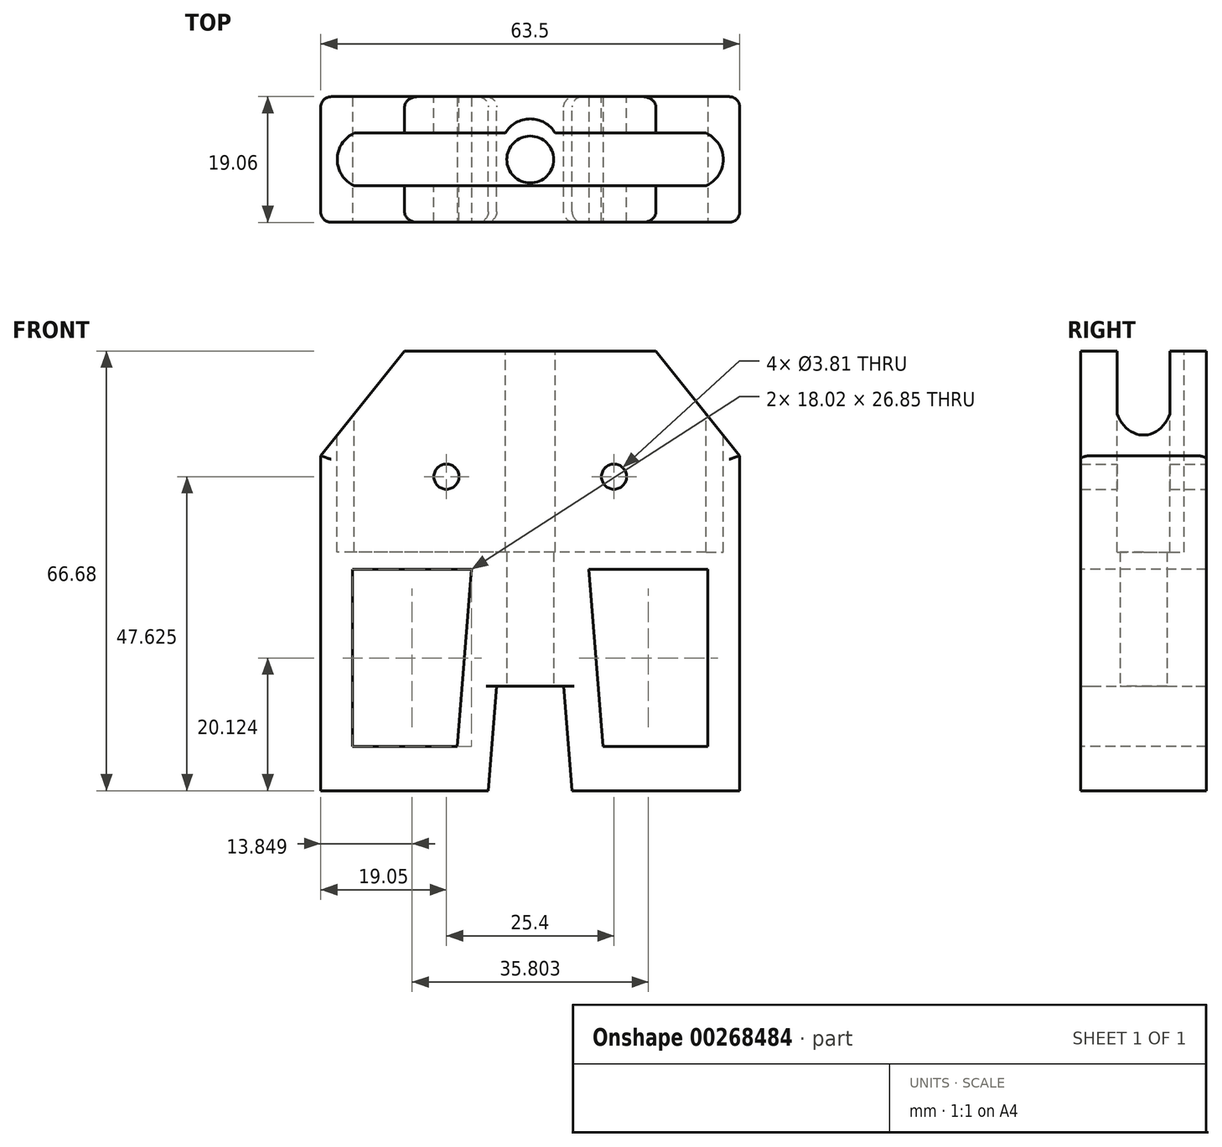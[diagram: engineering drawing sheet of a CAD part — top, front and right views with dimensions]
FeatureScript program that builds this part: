
annotation { "Feature Type Name" : "Feature", "Feature Type Description" : "" }
export const myFeature = defineFeature(function(context is Context, id is Id, definition is map)
    precondition{}
    {
        {
            var Q0;
            Q0=qCreatedBy(makeId("Front.planeOp"),FACE);
            var sketch = newSketch(context, id + "F0", { "sketchPlane" : qUnion([Q0])});
            skLineSegment(sketch, "E0", {"start": v(-31.75, 0) * mm, "end": v(-31.75, 50.8) * mm});
            skLineSegment(sketch, "E1", {"start": v(-31.75, 50.8) * mm, "end": v(-19.05, 66.68) * mm});
            skLineSegment(sketch, "E2", {"start": v(-19.05, 66.68) * mm, "end": v(0, 66.68) * mm});
            skLineSegment(sketch, "E3", {"start": v(0, 66.68) * mm, "end": v(0, 15.88) * mm});
            skLineSegment(sketch, "E4", {"start": v(-6.35, 0) * mm, "end": v(-31.75, 0) * mm});
            skLineSegment(sketch, "E5", {"start": v(0, 15.88) * mm, "end": v(-5.08, 15.88) * mm});
            skLineSegment(sketch, "E6", {"start": v(-5.08, 15.88) * mm, "end": v(-6.35, 0) * mm});
            skLineSegment(sketch, "E7.MirrorCS", {"start": v(19.05, 66.68) * mm, "end": v(0, 66.68) * mm});
            skLineSegment(sketch, "E8.MirrorCS", {"start": v(31.75, 50.8) * mm, "end": v(19.05, 66.68) * mm});
            skLineSegment(sketch, "E9.MirrorCS", {"start": v(31.75, 0) * mm, "end": v(31.75, 50.8) * mm});
            skLineSegment(sketch, "E10.MirrorCS", {"start": v(6.35, 0) * mm, "end": v(31.75, 0) * mm});
            skLineSegment(sketch, "E11.MirrorCS", {"start": v(5.08, 15.88) * mm, "end": v(6.35, 0) * mm});
            skLineSegment(sketch, "E12.MirrorCS", {"start": v(0, 15.88) * mm, "end": v(5.08, 15.88) * mm});
            skSolve(sketch);
        }
        {
            var Q0;
            Q0 = qSketchRegion(id + "F0", true);
            extrude(context, id + "F1", {"entities" : qUnion([Q0]), "endBound" : BoundingType.SYMMETRIC, "depth" : 19.05 * mm});
        }
        {
            var Q0;
            Q0=makeQuery(id+"F1.opExtrude","SWEPT_FACE",FACE,{"disambiguationData":[OSD([sQuery(id+"F0.wireOp",EDGE,"E2"),sQuery(id+"F0.wireOp",EDGE,"E7.MirrorCS")])]});
            var sketch = newSketch(context, id + "F2", { "sketchPlane" : qUnion([Q0])});
            skLineSegment(sketch, "E13.bottom", {"start": v(26.67, 4) * mm, "end": v(3.78, 4) * mm});
            skLineSegment(sketch, "E13.top", {"start": v(26.67, -4) * mm, "end": v(-26.67, -4) * mm});
            skLineSegment(sketch, "E13.left", {"start": v(26.67, 4) * mm, "end": v(26.67, -4) * mm});
            skLineSegment(sketch, "E13.right", {"start": v(-26.67, 4) * mm, "end": v(-26.67, -4) * mm});
            skPoint(sketch, "E13.middle", {"position": v(0, 0) * mm});
            skArc(sketch, "E14", {"start": v(-3.78, 4) * mm, "mid": v(0, 6.16) * mm, "end": v(3.78, 4) * mm});
            skLineSegment(sketch, "E15.trimOffspring", {"start": v(-3.78, 4) * mm, "end": v(-26.67, 4) * mm});
            skArc(sketch, "E16", {"start": v(-26.67, 4) * mm, "mid": v(-29.26, 0) * mm, "end": v(-26.67, -4) * mm});
            skArc(sketch, "E17", {"start": v(26.67, -4) * mm, "mid": v(29.26, 0) * mm, "end": v(26.67, 4) * mm});
            skSolve(sketch);
        }
        {
            var Q0;
            Q0 = qSketchRegion(id + "F2", true);
            extrude(context, id + "F3", {"entities" : qUnion([Q0]), "operationType" : NewBodyOperationType.REMOVE, "oppositeDirection" : true, "depth" : 30.48 * mm});
        }
        {
            var Q0;
            Q0=qCreatedBy(makeId("Top.planeOp"),FACE);
            var sketch = newSketch(context, id + "F4", { "sketchPlane" : qUnion([Q0])});
            skCircle(sketch, "E18", {"center": v(0, 0) * mm, "radius": 3.56 * mm});
            skSolve(sketch);
        }
        {
            var Q0;
            Q0 = qSketchRegion(id + "F4", true);
            var Q1;
            Q1=makeQuery(id+"F3.boolean.opBoolean","COPY",FACE,{"derivedFrom":makeQuery(id+"F3.opExtrude","CAP_FACE",FACE,{"disambiguationData":[OSD([sQuery(id+"F2.wireOp",EDGE,"E13.bottom"),sQuery(id+"F2.wireOp",EDGE,"E13.top"),sQuery(id+"F2.wireOp",EDGE,"E13.left"),sQuery(id+"F2.wireOp",EDGE,"E13.right"),sQuery(id+"F2.wireOp",EDGE,"E14"),sQuery(id+"F2.wireOp",EDGE,"E15.trimOffspring")])],"isStart":false})});
            extrude(context, id + "F5", {"entities" : qUnion([Q0]), "operationType" : NewBodyOperationType.REMOVE, "endBound" : BoundingType.UP_TO_SURFACE, "endBoundEntityFace" : qUnion([Q1]), "depth" : 50.8 * mm});
        }
        {
            var Q0;
            Q0=qCreatedBy(makeId("Front.planeOp"),FACE);
            var sketch = newSketch(context, id + "F6", { "sketchPlane" : qUnion([Q0])});
            skLineSegment(sketch, "E19", {"start": v(-26.91, 33.55) * mm, "end": v(-26.91, 6.7) * mm});
            skLineSegment(sketch, "E20", {"start": v(-26.91, 6.7) * mm, "end": v(-11.04, 6.7) * mm});
            skLineSegment(sketch, "E21", {"start": v(-11.04, 6.7) * mm, "end": v(-8.89, 33.55) * mm});
            skLineSegment(sketch, "E22", {"start": v(-8.9, 33.55) * mm, "end": v(-26.91, 33.55) * mm});
            skLineSegment(sketch, "E23.MirrorCS", {"start": v(11.04, 6.7) * mm, "end": v(8.89, 33.55) * mm});
            skLineSegment(sketch, "E24.MirrorCS", {"start": v(8.9, 33.55) * mm, "end": v(26.91, 33.55) * mm});
            skLineSegment(sketch, "E25.MirrorCS", {"start": v(26.91, 33.55) * mm, "end": v(26.91, 6.7) * mm});
            skLineSegment(sketch, "E26.MirrorCS", {"start": v(26.91, 6.7) * mm, "end": v(11.04, 6.7) * mm});
            skSolve(sketch);
        }
        {
            var Q0;
            Q0 = qSketchRegion(id + "F6", true);
            extrude(context, id + "F7", {"entities" : qUnion([Q0]), "operationType" : NewBodyOperationType.REMOVE, "endBound" : BoundingType.SYMMETRIC, "oppositeDirection" : true, "depth" : 25.4 * mm});
        }
        {
            var Q0;
            Q0=makeQuery(id+"F1.opExtrude","CAP_EDGE",EDGE,{"disambiguationData":[OSD([sQuery(id+"F0.wireOp",EDGE,"E9.MirrorCS")])],"isStart":true});
            var Q1;
            Q1=makeQuery(id+"F1.opExtrude","CAP_EDGE",EDGE,{"disambiguationData":[OSD([sQuery(id+"F0.wireOp",EDGE,"E8.MirrorCS")])],"isStart":true});
            var Q2;
            Q2=makeQuery(id+"F1.opExtrude","CAP_EDGE",EDGE,{"disambiguationData":[OSD([sQuery(id+"F0.wireOp",EDGE,"E9.MirrorCS")])],"isStart":false});
            var Q3;
            Q3=makeQuery(id+"F1.opExtrude","CAP_EDGE",EDGE,{"disambiguationData":[OSD([sQuery(id+"F0.wireOp",EDGE,"E8.MirrorCS")])],"isStart":false});
            var Q4;
            Q4=makeQuery(id+"F1.opExtrude","CAP_EDGE",EDGE,{"disambiguationData":[OSD([sQuery(id+"F0.wireOp",EDGE,"E11.MirrorCS")])],"isStart":true});
            var Q5;
            Q5=makeQuery(id+"F1.opExtrude","CAP_EDGE",EDGE,{"disambiguationData":[OSD([sQuery(id+"F0.wireOp",EDGE,"E11.MirrorCS")])],"isStart":false});
            var Q6;
            Q6=makeQuery(id+"F1.opExtrude","CAP_EDGE",EDGE,{"disambiguationData":[OSD([sQuery(id+"F0.wireOp",EDGE,"E6")])],"isStart":false});
            var Q7;
            Q7=makeQuery(id+"F1.opExtrude","CAP_EDGE",EDGE,{"disambiguationData":[OSD([sQuery(id+"F0.wireOp",EDGE,"E6")])],"isStart":true});
            var Q8;
            Q8=makeQuery(id+"F1.opExtrude","CAP_EDGE",EDGE,{"disambiguationData":[OSD([sQuery(id+"F0.wireOp",EDGE,"E0")])],"isStart":true});
            var Q9;
            Q9=makeQuery(id+"F1.opExtrude","CAP_EDGE",EDGE,{"disambiguationData":[OSD([sQuery(id+"F0.wireOp",EDGE,"E0")])],"isStart":false});
            var Q10;
            Q10=makeQuery(id+"F1.opExtrude","CAP_EDGE",EDGE,{"disambiguationData":[OSD([sQuery(id+"F0.wireOp",EDGE,"E1")])],"isStart":true});
            var Q11;
            Q11=makeQuery(id+"F1.opExtrude","CAP_EDGE",EDGE,{"disambiguationData":[OSD([sQuery(id+"F0.wireOp",EDGE,"E1")])],"isStart":false});
            var Q12;
            Q12=makeQuery(id+"F7.boolean.opBoolean","INTERSECT",EDGE,{"derivedFrom":[makeQuery(id+"F1.opExtrude","CAP_FACE",FACE,{"disambiguationData":[OSD([sQuery(id+"F0.wireOp",EDGE,"E0"),sQuery(id+"F0.wireOp",EDGE,"E1"),sQuery(id+"F0.wireOp",EDGE,"E2"),sQuery(id+"F0.wireOp",EDGE,"E4"),sQuery(id+"F0.wireOp",EDGE,"E5"),sQuery(id+"F0.wireOp",EDGE,"E6"),sQuery(id+"F0.wireOp",EDGE,"E8.MirrorCS"),sQuery(id+"F0.wireOp",EDGE,"E7.MirrorCS"),sQuery(id+"F0.wireOp",EDGE,"E9.MirrorCS"),sQuery(id+"F0.wireOp",EDGE,"E10.MirrorCS"),sQuery(id+"F0.wireOp",EDGE,"E11.MirrorCS"),sQuery(id+"F0.wireOp",EDGE,"E12.MirrorCS")])],"isStart":false}),makeQuery(id+"F7.opExtrude","SWEPT_FACE",FACE,{"disambiguationData":[OSD([sQuery(id+"F6.wireOp",EDGE,"b008d278-9569-4f77-97fc-4aec5f2cc1fe")])]})]});
            var Q13;
            Q13=makeQuery(id+"F7.boolean.opBoolean","INTERSECT",EDGE,{"derivedFrom":[makeQuery(id+"F1.opExtrude","CAP_FACE",FACE,{"disambiguationData":[OSD([sQuery(id+"F0.wireOp",EDGE,"E0"),sQuery(id+"F0.wireOp",EDGE,"E1"),sQuery(id+"F0.wireOp",EDGE,"E2"),sQuery(id+"F0.wireOp",EDGE,"E4"),sQuery(id+"F0.wireOp",EDGE,"E5"),sQuery(id+"F0.wireOp",EDGE,"E6"),sQuery(id+"F0.wireOp",EDGE,"E8.MirrorCS"),sQuery(id+"F0.wireOp",EDGE,"E7.MirrorCS"),sQuery(id+"F0.wireOp",EDGE,"E9.MirrorCS"),sQuery(id+"F0.wireOp",EDGE,"E10.MirrorCS"),sQuery(id+"F0.wireOp",EDGE,"E11.MirrorCS"),sQuery(id+"F0.wireOp",EDGE,"E12.MirrorCS")])],"isStart":true}),makeQuery(id+"F7.opExtrude","SWEPT_FACE",FACE,{"disambiguationData":[OSD([sQuery(id+"F6.wireOp",EDGE,"b008d278-9569-4f77-97fc-4aec5f2cc1fe")])]})]});
            var Q14;
            Q14=makeQuery(id+"F7.boolean.opBoolean","INTERSECT",EDGE,{"derivedFrom":[makeQuery(id+"F1.opExtrude","CAP_FACE",FACE,{"disambiguationData":[OSD([sQuery(id+"F0.wireOp",EDGE,"E0"),sQuery(id+"F0.wireOp",EDGE,"E1"),sQuery(id+"F0.wireOp",EDGE,"E2"),sQuery(id+"F0.wireOp",EDGE,"E4"),sQuery(id+"F0.wireOp",EDGE,"E5"),sQuery(id+"F0.wireOp",EDGE,"E6"),sQuery(id+"F0.wireOp",EDGE,"E8.MirrorCS"),sQuery(id+"F0.wireOp",EDGE,"E7.MirrorCS"),sQuery(id+"F0.wireOp",EDGE,"E9.MirrorCS"),sQuery(id+"F0.wireOp",EDGE,"E10.MirrorCS"),sQuery(id+"F0.wireOp",EDGE,"E11.MirrorCS"),sQuery(id+"F0.wireOp",EDGE,"E12.MirrorCS")])],"isStart":false}),makeQuery(id+"F7.opExtrude","SWEPT_FACE",FACE,{"disambiguationData":[OSD([sQuery(id+"F6.wireOp",EDGE,"ad2d7e54-11d6-474b-a721-59a2615fd2a70.MirrorC")])]})]});
            var Q15;
            Q15=makeQuery(id+"F7.boolean.opBoolean","INTERSECT",EDGE,{"derivedFrom":[makeQuery(id+"F1.opExtrude","CAP_FACE",FACE,{"disambiguationData":[OSD([sQuery(id+"F0.wireOp",EDGE,"E0"),sQuery(id+"F0.wireOp",EDGE,"E1"),sQuery(id+"F0.wireOp",EDGE,"E2"),sQuery(id+"F0.wireOp",EDGE,"E4"),sQuery(id+"F0.wireOp",EDGE,"E5"),sQuery(id+"F0.wireOp",EDGE,"E6"),sQuery(id+"F0.wireOp",EDGE,"E8.MirrorCS"),sQuery(id+"F0.wireOp",EDGE,"E7.MirrorCS"),sQuery(id+"F0.wireOp",EDGE,"E9.MirrorCS"),sQuery(id+"F0.wireOp",EDGE,"E10.MirrorCS"),sQuery(id+"F0.wireOp",EDGE,"E11.MirrorCS"),sQuery(id+"F0.wireOp",EDGE,"E12.MirrorCS")])],"isStart":true}),makeQuery(id+"F7.opExtrude","SWEPT_FACE",FACE,{"disambiguationData":[OSD([sQuery(id+"F6.wireOp",EDGE,"ad2d7e54-11d6-474b-a721-59a2615fd2a70.MirrorC")])]})]});
            fillet(context, id + "F8", {"entities" : qUnion([Q0, Q1, Q2, Q3, Q4, Q5, Q6, Q7, Q8, Q9, Q10, Q11, Q12, Q13, Q14, Q15]), "radius" : 1.59 * mm, "tangentPropagation" : true, "allowEdgeOverflow" : false});
        }
        {
            var Q0;
            Q0=makeQuery(id+"F1.opExtrude","CAP_FACE",FACE,{"disambiguationData":[OSD([sQuery(id+"F0.wireOp",EDGE,"E0"),sQuery(id+"F0.wireOp",EDGE,"E1"),sQuery(id+"F0.wireOp",EDGE,"E2"),sQuery(id+"F0.wireOp",EDGE,"E4"),sQuery(id+"F0.wireOp",EDGE,"E5"),sQuery(id+"F0.wireOp",EDGE,"E6"),sQuery(id+"F0.wireOp",EDGE,"E8.MirrorCS"),sQuery(id+"F0.wireOp",EDGE,"E7.MirrorCS"),sQuery(id+"F0.wireOp",EDGE,"E9.MirrorCS"),sQuery(id+"F0.wireOp",EDGE,"E10.MirrorCS"),sQuery(id+"F0.wireOp",EDGE,"E11.MirrorCS"),sQuery(id+"F0.wireOp",EDGE,"E12.MirrorCS")])],"isStart":true});
            var sketch = newSketch(context, id + "F9", { "sketchPlane" : qUnion([Q0])});
            skCircle(sketch, "E27", {"center": v(-12.7, 47.63) * mm, "radius": 1.9 * mm});
            skCircle(sketch, "E28", {"center": v(12.7, 47.63) * mm, "radius": 1.9 * mm});
            skSolve(sketch);
        }
        {
            var Q0;
            Q0 = qSketchRegion(id + "F9", true);
            var Q1;
            Q1=makeQuery(id+"F1.opExtrude","CAP_FACE",FACE,{"disambiguationData":[OSD([sQuery(id+"F0.wireOp",EDGE,"E0"),sQuery(id+"F0.wireOp",EDGE,"E1"),sQuery(id+"F0.wireOp",EDGE,"E2"),sQuery(id+"F0.wireOp",EDGE,"E4"),sQuery(id+"F0.wireOp",EDGE,"E5"),sQuery(id+"F0.wireOp",EDGE,"E6"),sQuery(id+"F0.wireOp",EDGE,"E8.MirrorCS"),sQuery(id+"F0.wireOp",EDGE,"E7.MirrorCS"),sQuery(id+"F0.wireOp",EDGE,"E9.MirrorCS"),sQuery(id+"F0.wireOp",EDGE,"E10.MirrorCS"),sQuery(id+"F0.wireOp",EDGE,"E11.MirrorCS"),sQuery(id+"F0.wireOp",EDGE,"E12.MirrorCS")])],"isStart":false});
            extrude(context, id + "F10", {"entities" : qUnion([Q0]), "operationType" : NewBodyOperationType.REMOVE, "endBound" : BoundingType.UP_TO_SURFACE, "oppositeDirection" : true, "endBoundEntityFace" : qUnion([Q1]), "depth" : 25.4 * mm});
        }
    });
